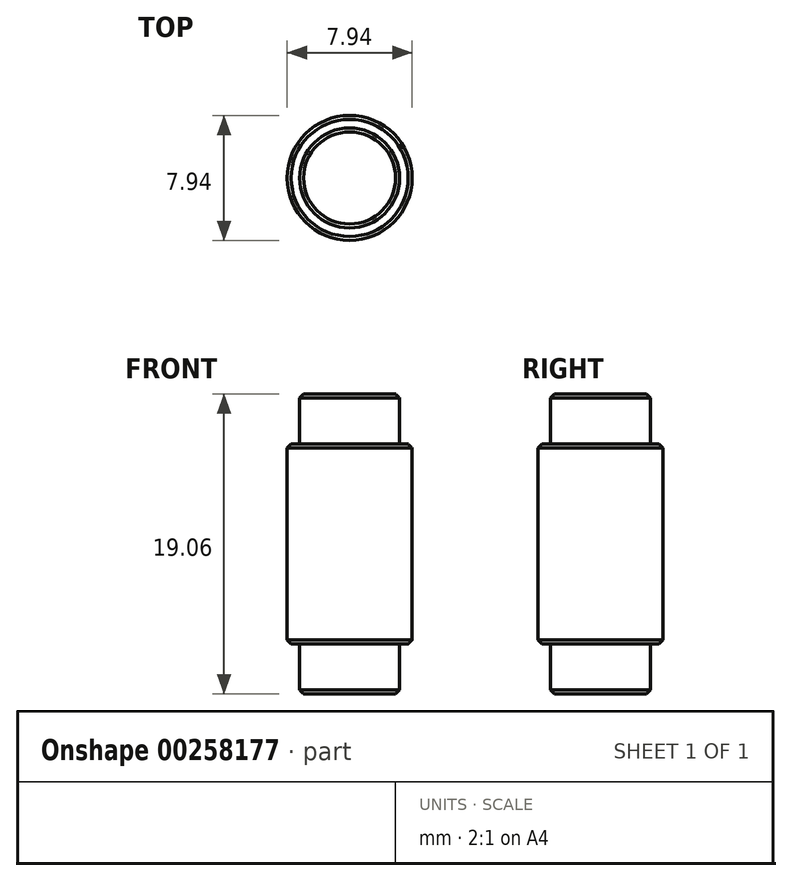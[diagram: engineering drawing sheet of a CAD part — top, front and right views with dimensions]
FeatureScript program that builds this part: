
annotation { "Feature Type Name" : "Feature", "Feature Type Description" : "" }
export const myFeature = defineFeature(function(context is Context, id is Id, definition is map)
    precondition{}
    {
        {
            var Q0;
            Q0=qCreatedBy(makeId("Top.planeOp"),FACE);
            var sketch = newSketch(context, id + "F0", { "sketchPlane" : qUnion([Q0])});
            skCircle(sketch, "E0", {"center": v(0, 0) * mm, "radius": 3.97 * mm});
            skSolve(sketch);
        }
        {
            var Q0;
            Q0=makeQuery(id+"F0.imprint","IMPRINT",FACE,{"disambiguationData":[TD([[makeQuery(id+"F0.imprint","IMPRINT",EDGE,{"derivedFrom":sQuery(id+"F0.wireOp",EDGE,"E0")}),1.0]])]});
            extrude(context, id + "F1", {"entities" : qUnion([Q0]), "depth" : 12.7 * mm});
        }
        {
            var Q0;
            Q0=makeQuery(id+"F1.opExtrude","CAP_FACE",FACE,{"disambiguationData":[OSD([sQuery(id+"F0.wireOp",EDGE,"E0")])],"isStart":false});
            var sketch = newSketch(context, id + "F2", { "sketchPlane" : qUnion([Q0])});
            skCircle(sketch, "E1", {"center": v(0, 0) * mm, "radius": 3.18 * mm});
            skSolve(sketch);
        }
        {
            var Q0;
            Q0=makeQuery(id+"F2.imprint","IMPRINT",FACE,{"disambiguationData":[TD([[makeQuery(id+"F2.imprint","IMPRINT",EDGE,{"derivedFrom":sQuery(id+"F2.wireOp",EDGE,"E1")}),1.0]])]});
            extrude(context, id + "F3", {"entities" : qUnion([Q0]), "operationType" : NewBodyOperationType.ADD, "depth" : 3.17 * mm});
        }
        {
            var Q0;
            Q0=makeQuery(id+"F1.opExtrude","CAP_FACE",FACE,{"disambiguationData":[OSD([sQuery(id+"F0.wireOp",EDGE,"E0")])],"isStart":true});
            var sketch = newSketch(context, id + "F4", { "sketchPlane" : qUnion([Q0])});
            skCircle(sketch, "E2", {"center": v(0, 0) * mm, "radius": 3.18 * mm});
            skSolve(sketch);
        }
        {
            var Q0;
            Q0=makeQuery(id+"F4.imprint","IMPRINT",FACE,{"disambiguationData":[TD([[makeQuery(id+"F4.imprint","IMPRINT",EDGE,{"derivedFrom":sQuery(id+"F4.wireOp",EDGE,"E2")}),1.0]])]});
            extrude(context, id + "F5", {"entities" : qUnion([Q0]), "operationType" : NewBodyOperationType.ADD, "depth" : 3.17 * mm});
        }
        {
            var Q0;
            Q0=makeQuery(id+"F5.opExtrude","CAP_EDGE",EDGE,{"disambiguationData":[OSD([sQuery(id+"F4.wireOp",EDGE,"E2")])],"isStart":false});
            var Q1;
            Q1=makeQuery(id+"F1.opExtrude","CAP_EDGE",EDGE,{"disambiguationData":[OSD([sQuery(id+"F0.wireOp",EDGE,"E0")])],"isStart":true});
            var Q2;
            Q2=makeQuery(id+"F3.opExtrude","CAP_EDGE",EDGE,{"disambiguationData":[OSD([sQuery(id+"F2.wireOp",EDGE,"E1")])],"isStart":false});
            var Q3;
            Q3=makeQuery(id+"F1.opExtrude","CAP_EDGE",EDGE,{"disambiguationData":[OSD([sQuery(id+"F0.wireOp",EDGE,"E0")])],"isStart":false});
            chamfer(context, id + "F6", {"entities" : qUnion([Q0, Q1, Q2, Q3]), "width" : 0.25 * mm, "tangentPropagation" : true});
        }
    });
